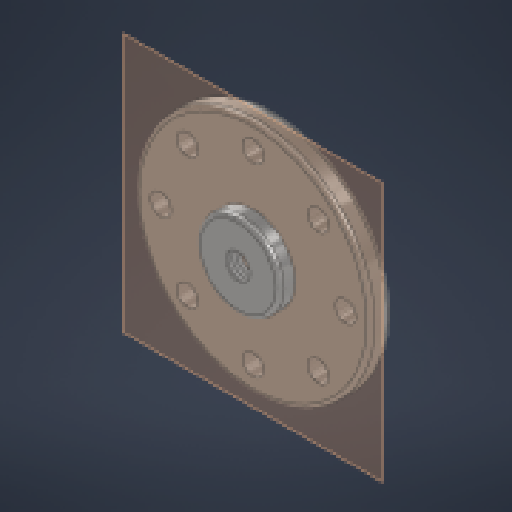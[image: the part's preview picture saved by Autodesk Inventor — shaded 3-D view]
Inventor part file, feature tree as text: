
AUTODESK INVENTOR PART (.ipt)
format: ipt  version: 2024 (Build 280153000, 153)  size: 223,744 bytes
history: native  units: mm
features: other x15, sketch x3, extrude x3, fillet x2, reference x2, chamfer x1, projected_geometry x1
ambient origin geometry x8: Origin, YZ Plane, XZ Plane, XY Plane, X Axis, Y Axis, Z Axis, Center Point
bodies: Body1 (feature_tree)
feature tree (27):
  other  "솔리드1"
  other  "작업 평면1"
  sketch  "스케치1"
  other  "작업 평면2"
  extrude  "돌출1"  Depth=10.0mm TaperAngle=0.0deg
  sketch  "스케치2"
  other  "작업 평면3"
  extrude  "돌출2"  Depth=3.0mm
  extrude  "돌출3"  Depth=10.0mm TaperAngle=0.0deg
  other  "스레드1"
  fillet  "모깎기1"  [1 undecoded]
  fillet  "모깎기2"  Radius=4.3mm
  other  "스레드2"
  other  "스레드3"
  other  "스레드4"
  other  "스레드5"
  other  "스레드6"
  other  "스레드7"
  other  "스레드8"
  other  "스레드9"
  chamfer  "모따기1"  Distance=0.1mm
  reference  "참조1"
  reference  "참조2"
  sketch  "스케치3"
  projected_geometry  "투영된 루프1"
  other  "Roll_Fixation_Set.iam"
  other  "MX-64T:2"
note: 1 required parameter value undecoded (feature->parameter linkage not recoverable at this tier; creation-order binding heuristic only, values carry confidence <= 0.55)
